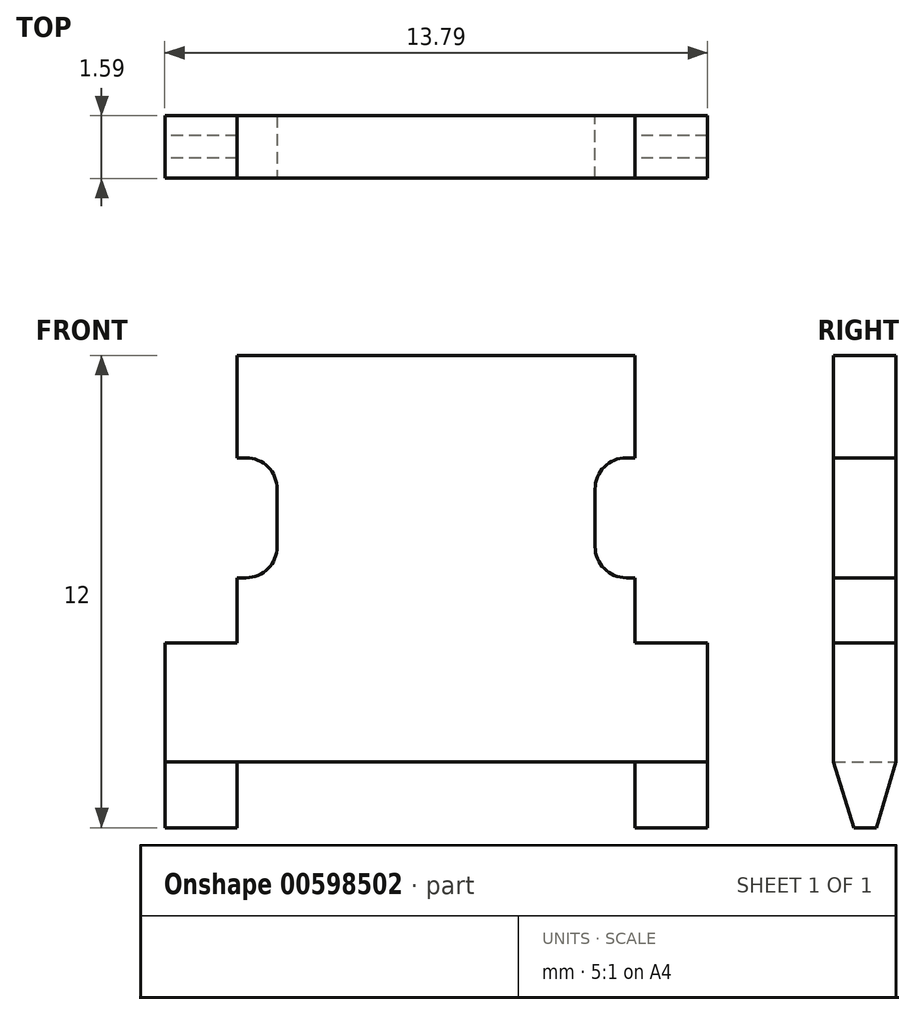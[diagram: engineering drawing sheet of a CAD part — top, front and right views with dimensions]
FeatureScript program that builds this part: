
annotation { "Feature Type Name" : "Feature", "Feature Type Description" : "" }
export const myFeature = defineFeature(function(context is Context, id is Id, definition is map)
    precondition{}
    {
        {
            var Q0;
            Q0=qCreatedBy(makeId("Front.planeOp"),FACE);
            var sketch = newSketch(context, id + "F0", { "sketchPlane" : qUnion([Q0])});
            skLineSegment(sketch, "E0", {"start": v(-11.97, 0) * mm, "end": v(-11.97, 7.55) * mm});
            skLineSegment(sketch, "E1", {"start": v(-11.97, 7.55) * mm, "end": v(-1.86, 7.55) * mm});
            skLineSegment(sketch, "E2", {"start": v(-1.86, 7.55) * mm, "end": v(-1.86, 0) * mm});
            skLineSegment(sketch, "E3", {"start": v(-1.86, 0) * mm, "end": v(-0.02, 0) * mm});
            skLineSegment(sketch, "E4", {"start": v(-0.02, 0) * mm, "end": v(-0.02, -4.7) * mm});
            skLineSegment(sketch, "E5", {"start": v(-0.02, -4.7) * mm, "end": v(-1.86, -4.7) * mm});
            skLineSegment(sketch, "E6", {"start": v(-1.86, -4.7) * mm, "end": v(-1.86, -3.03) * mm});
            skLineSegment(sketch, "E7", {"start": v(-11.97, -3.03) * mm, "end": v(-11.97, -4.7) * mm});
            skLineSegment(sketch, "E8", {"start": v(-11.97, -4.7) * mm, "end": v(-13.8, -4.7) * mm});
            skLineSegment(sketch, "E9", {"start": v(-13.8, -4.7) * mm, "end": v(-13.8, 0) * mm});
            skLineSegment(sketch, "E10", {"start": v(-13.8, 0) * mm, "end": v(-11.97, 0) * mm});
            skLineSegment(sketch, "E11", {"start": v(-11.97, -3.03) * mm, "end": v(-1.86, -3.03) * mm});
            skSolve(sketch);
        }
        {
            var Q0;
            Q0=makeQuery(id+"F0.imprint","IMPRINT",FACE,{"disambiguationData":[TD([[makeQuery(id+"F0.imprint","IMPRINT",EDGE,{"derivedFrom":sQuery(id+"F0.wireOp",EDGE,"E0")}),-1.0]])]});
            extrude(context, id + "F1", {"entities" : qUnion([Q0]), "depth" : 1.59 * mm, "offsetDistance" : 25.4 * mm});
        }
        {
            var Q0;
            Q0=makeQuery(id+"F1.opExtrude","SWEPT_FACE",FACE,{"disambiguationData":[OSD([sQuery(id+"F0.wireOp",EDGE,"E9")])]});
            var sketch = newSketch(context, id + "F2", { "sketchPlane" : qUnion([Q0])});
            skLineSegment(sketch, "E12", {"start": v(0, -3.02) * mm, "end": v(0.5, -4.7) * mm});
            skLineSegment(sketch, "E13", {"start": v(0.5, -4.7) * mm, "end": v(1.08, -4.7) * mm});
            skLineSegment(sketch, "E14", {"start": v(1.08, -4.7) * mm, "end": v(1.59, -3.02) * mm});
            skSolve(sketch);
        }
        {
            var Q0;
            {var subQ0=sQuery(id+"F2.wireOp",EDGE,"E12");Q0=makeQuery(id+"F2.imprint","IMPRINT",FACE,{"disambiguationData":[TD([[makeQuery(id+"F2.imprint","IMPRINT",EDGE,{"derivedFrom":subQ0}),-1.0]])]});}
            var Q1;
            {var subQ0=sQuery(id+"F2.wireOp",EDGE,"E14");Q1=makeQuery(id+"F2.imprint","IMPRINT",FACE,{"disambiguationData":[TD([[makeQuery(id+"F2.imprint","IMPRINT",EDGE,{"derivedFrom":subQ0}),-1.0]])]});}
            extrude(context, id + "F3", {"entities" : qUnion([Q0, Q1]), "operationType" : NewBodyOperationType.REMOVE, "oppositeDirection" : true, "depth" : 25.4 * mm, "offsetDistance" : 25.4 * mm});
        }
        {
            var Q0;
            Q0=makeQuery(id+"F1.opExtrude","SWEPT_FACE",FACE,{"disambiguationData":[OSD([sQuery(id+"F0.wireOp",EDGE,"E2")])]});
            var sketch = newSketch(context, id + "F4", { "sketchPlane" : qUnion([Q0])});
            skLineSegment(sketch, "E15", {"start": v(-1.59, 4.7) * mm, "end": v(0, 4.7) * mm});
            skLineSegment(sketch, "E16", {"start": v(-1.59, 1.65) * mm, "end": v(0, 1.65) * mm});
            skSolve(sketch);
        }
        {
            var Q0;
            {var subQ0=sQuery(id+"F4.wireOp",EDGE,"E15");Q0=makeQuery(id+"F4.imprint","IMPRINT",FACE,{"disambiguationData":[TD([[makeQuery(id+"F4.imprint","IMPRINT",EDGE,{"derivedFrom":subQ0}),-1.0]])]});}
            extrude(context, id + "F5", {"entities" : qUnion([Q0]), "operationType" : NewBodyOperationType.REMOVE, "oppositeDirection" : true, "depth" : 1.02 * mm, "offsetDistance" : 25.4 * mm});
        }
        {
            var Q0;
            Q0=makeQuery(id+"F5.boolean.opBoolean","COPY",EDGE,{"derivedFrom":makeQuery(id+"F5.opExtrude","CAP_EDGE",EDGE,{"disambiguationData":[OSD([sQuery(id+"F4.wireOp",EDGE,"E15")])],"isStart":false})});
            var Q1;
            Q1=makeQuery(id+"F5.boolean.opBoolean","COPY",EDGE,{"derivedFrom":makeQuery(id+"F5.opExtrude","CAP_EDGE",EDGE,{"disambiguationData":[OSD([sQuery(id+"F4.wireOp",EDGE,"E16")])],"isStart":false})});
            fillet(context, id + "F6", {"entities" : qUnion([Q0, Q1]), "radius" : 0.8 * mm, "tangentPropagation" : true, "allowEdgeOverflow" : false});
        }
        {
            var Q0;
            Q0=makeQuery(id+"F1.opExtrude","SWEPT_FACE",FACE,{"disambiguationData":[OSD([sQuery(id+"F0.wireOp",EDGE,"E0")])]});
            var sketch = newSketch(context, id + "F7", { "sketchPlane" : qUnion([Q0])});
            skLineSegment(sketch, "E17", {"start": v(0, 1.65) * mm, "end": v(1.59, 1.65) * mm});
            skLineSegment(sketch, "E18", {"start": v(0, 4.7) * mm, "end": v(1.59, 4.7) * mm});
            skSolve(sketch);
        }
        {
            var Q0;
            {var subQ0=sQuery(id+"F7.wireOp",EDGE,"E17");Q0=makeQuery(id+"F7.imprint","IMPRINT",FACE,{"disambiguationData":[TD([[makeQuery(id+"F7.imprint","IMPRINT",EDGE,{"derivedFrom":subQ0}),1.0]])]});}
            extrude(context, id + "F8", {"entities" : qUnion([Q0]), "operationType" : NewBodyOperationType.REMOVE, "oppositeDirection" : true, "depth" : 1.02 * mm, "offsetDistance" : 25.4 * mm});
        }
        {
            var Q0;
            Q0=makeQuery(id+"F8.boolean.opBoolean","COPY",EDGE,{"derivedFrom":makeQuery(id+"F8.opExtrude","CAP_EDGE",EDGE,{"disambiguationData":[OSD([sQuery(id+"F7.wireOp",EDGE,"E18")])],"isStart":false})});
            var Q1;
            Q1=makeQuery(id+"F8.boolean.opBoolean","COPY",EDGE,{"derivedFrom":makeQuery(id+"F8.opExtrude","CAP_EDGE",EDGE,{"disambiguationData":[OSD([sQuery(id+"F7.wireOp",EDGE,"E17")])],"isStart":false})});
            fillet(context, id + "F9", {"entities" : qUnion([Q0, Q1]), "radius" : 0.8 * mm, "tangentPropagation" : true, "allowEdgeOverflow" : false});
        }
        {
            var Q0;
            Q0=makeQuery(id+"F1.opExtrude","SWEPT_FACE",FACE,{"disambiguationData":[OSD([sQuery(id+"F0.wireOp",EDGE,"E1")])]});
            extrude(context, id + "F10", {"entities" : qUnion([Q0]), "operationType" : NewBodyOperationType.REMOVE, "oppositeDirection" : true, "depth" : 0.25 * mm, "offsetDistance" : 25.4 * mm});
        }
    });
